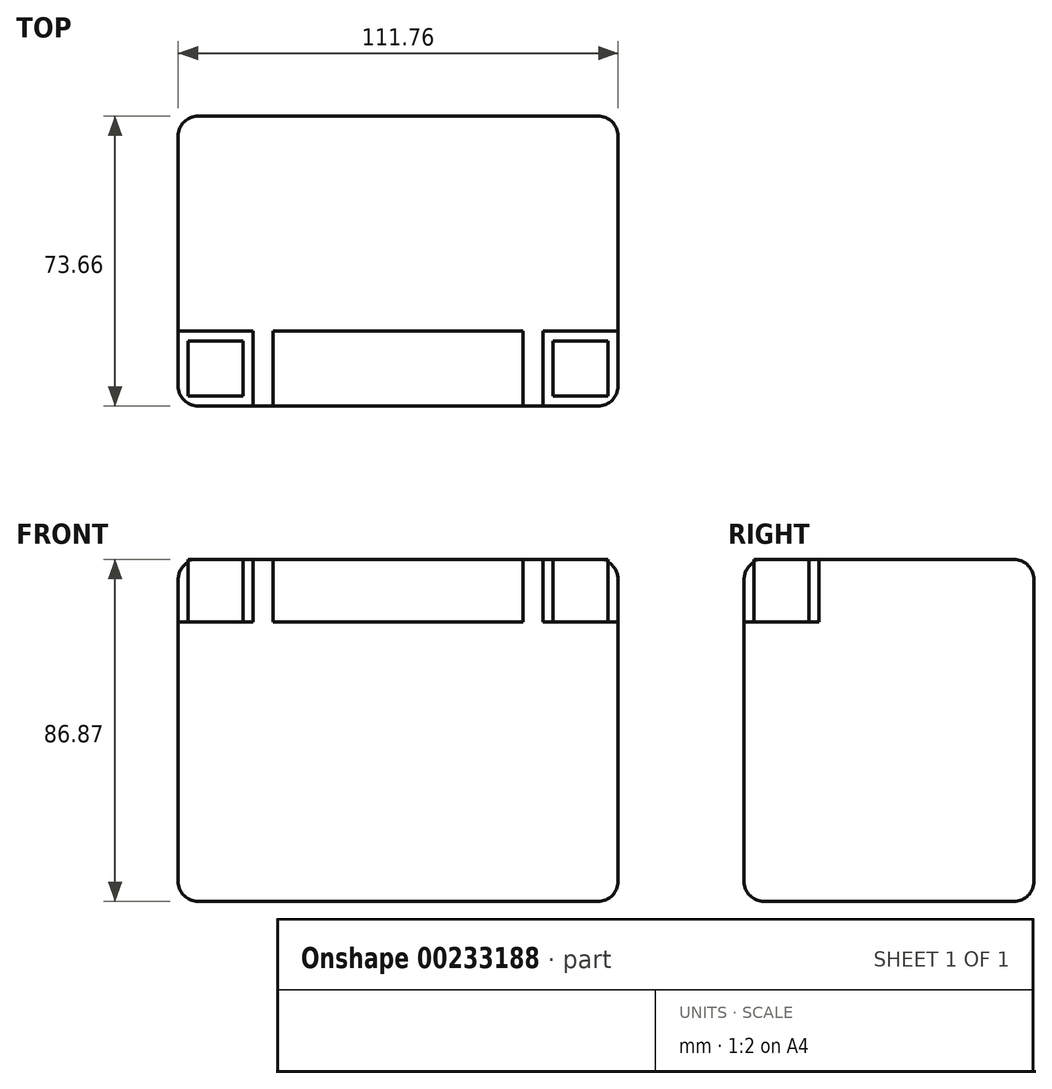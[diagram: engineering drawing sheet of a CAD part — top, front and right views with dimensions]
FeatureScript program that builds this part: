
annotation { "Feature Type Name" : "Feature", "Feature Type Description" : "" }
export const myFeature = defineFeature(function(context is Context, id is Id, definition is map)
    precondition{}
    {
        {
            var Q0;
            Q0=qCreatedBy(makeId("Top.planeOp"),FACE);
            var sketch = newSketch(context, id + "F0", { "sketchPlane" : qUnion([Q0])});
            skLineSegment(sketch, "E0.bottom", {"start": v(55.88, 36.83) * mm, "end": v(-55.88, 36.83) * mm});
            skLineSegment(sketch, "E0.top", {"start": v(55.88, -36.83) * mm, "end": v(-55.88, -36.83) * mm});
            skLineSegment(sketch, "E0.left", {"start": v(55.88, 36.83) * mm, "end": v(55.88, -36.83) * mm});
            skLineSegment(sketch, "E0.right", {"start": v(-55.88, 36.83) * mm, "end": v(-55.88, -36.83) * mm});
            skPoint(sketch, "E0.middle", {"position": v(0, 0) * mm});
            skSolve(sketch);
        }
        {
            var Q0;
            Q0 = qSketchRegion(id + "F0", true);
            extrude(context, id + "F1", {"entities" : qUnion([Q0]), "depth" : 86.87 * mm});
        }
        {
            var Q0;
            Q0=makeQuery(id+"F1.opExtrude","CAP_FACE",FACE,{"disambiguationData":[OSD([sQuery(id+"F0.wireOp",EDGE,"E0.bottom"),sQuery(id+"F0.wireOp",EDGE,"E0.top"),sQuery(id+"F0.wireOp",EDGE,"E0.left"),sQuery(id+"F0.wireOp",EDGE,"E0.right")])],"isStart":false});
            var sketch = newSketch(context, id + "F2", { "sketchPlane" : qUnion([Q0])});
            skLineSegment(sketch, "E1.bottom", {"start": v(-55.88, -36.83) * mm, "end": v(-36.83, -36.83) * mm});
            skLineSegment(sketch, "E1.top", {"start": v(-55.88, -17.78) * mm, "end": v(-36.83, -17.78) * mm});
            skLineSegment(sketch, "E1.left", {"start": v(-55.88, -36.83) * mm, "end": v(-55.88, -17.78) * mm});
            skLineSegment(sketch, "E1.right", {"start": v(-36.83, -36.83) * mm, "end": v(-36.83, -17.78) * mm});
            skLineSegment(sketch, "E2.bottom", {"start": v(-31.75, -36.83) * mm, "end": v(31.75, -36.83) * mm});
            skLineSegment(sketch, "E2.top", {"start": v(-31.75, -17.78) * mm, "end": v(31.75, -17.78) * mm});
            skLineSegment(sketch, "E2.left", {"start": v(-31.75, -36.83) * mm, "end": v(-31.75, -17.78) * mm});
            skLineSegment(sketch, "E2.right", {"start": v(31.75, -36.83) * mm, "end": v(31.75, -17.78) * mm});
            skLineSegment(sketch, "E3", {"start": v(0, 36.83) * mm, "end": v(0, -59.31) * mm, "construction": true});
            skPoint(sketch, "E3.endSnap0", {"position": v(0, -36.83) * mm});
            skLineSegment(sketch, "E4.bottom", {"start": v(-53.34, -34.3) * mm, "end": v(-39.37, -34.3) * mm});
            skLineSegment(sketch, "E4.top", {"start": v(-53.34, -20.32) * mm, "end": v(-39.37, -20.32) * mm});
            skLineSegment(sketch, "E4.left", {"start": v(-53.34, -34.3) * mm, "end": v(-53.34, -20.32) * mm});
            skLineSegment(sketch, "E4.right", {"start": v(-39.37, -34.3) * mm, "end": v(-39.37, -20.32) * mm});
            skLineSegment(sketch, "E5", {"start": v(-46.35, -17.78) * mm, "end": v(-46.35, -20.32) * mm, "construction": true});
            skLineSegment(sketch, "E6", {"start": v(-39.37, -27.3) * mm, "end": v(-36.83, -27.3) * mm, "construction": true});
            skLineSegment(sketch, "E7.MirrorCS", {"start": v(55.88, -17.78) * mm, "end": v(36.83, -17.78) * mm});
            skLineSegment(sketch, "E8.MirrorCS", {"start": v(36.83, -36.83) * mm, "end": v(36.83, -17.78) * mm});
            skLineSegment(sketch, "E9.MirrorCS", {"start": v(55.88, -36.83) * mm, "end": v(36.83, -36.83) * mm});
            skLineSegment(sketch, "E10.MirrorCS", {"start": v(55.88, -36.83) * mm, "end": v(55.88, -17.78) * mm});
            skLineSegment(sketch, "E11.MirrorCS", {"start": v(53.34, -34.29) * mm, "end": v(53.34, -20.32) * mm});
            skLineSegment(sketch, "E12.MirrorCS", {"start": v(53.34, -20.32) * mm, "end": v(39.37, -20.32) * mm});
            skLineSegment(sketch, "E13.MirrorCS", {"start": v(39.37, -34.29) * mm, "end": v(39.37, -20.32) * mm});
            skLineSegment(sketch, "E14.MirrorCS", {"start": v(53.34, -34.29) * mm, "end": v(39.37, -34.29) * mm});
            skSolve(sketch);
        }
        {
            var Q0;
            Q0 = qSketchRegion(id + "F2", true);
            extrude(context, id + "F3", {"entities" : qUnion([Q0]), "operationType" : NewBodyOperationType.REMOVE, "oppositeDirection" : true, "depth" : 15.88 * mm});
        }
        {
            var Q0;
            {var subQ0=sQuery(id+"F0.wireOp",EDGE,"E0.top");Q0=makeQuery(id+"F3.boolean.opBoolean","SPLIT",EDGE,{"disambiguationData":[TD([makeQuery(id+"F3.opExtrude","SWEPT_FACE",FACE,{"disambiguationData":[OSD([sQuery(id+"F2.wireOp",EDGE,"E1.right")])]})])],"derivedFrom":makeQuery(id+"F1.opExtrude","CAP_EDGE",EDGE,{"disambiguationData":[OSD([subQ0])],"isStart":false})});}
            var Q1;
            {var subQ0=sQuery(id+"F0.wireOp",EDGE,"E0.top");Q1=makeQuery(id+"F3.boolean.opBoolean","SPLIT",EDGE,{"disambiguationData":[TD([makeQuery(id+"F3.opExtrude","SWEPT_FACE",FACE,{"disambiguationData":[OSD([sQuery(id+"F2.wireOp",EDGE,"E2.right")])]})])],"derivedFrom":makeQuery(id+"F1.opExtrude","CAP_EDGE",EDGE,{"disambiguationData":[OSD([subQ0])],"isStart":false})});}
            var Q2;
            Q2=makeQuery(id+"F1.opExtrude","CAP_EDGE",EDGE,{"disambiguationData":[OSD([sQuery(id+"F0.wireOp",EDGE,"E0.left")])],"isStart":false});
            var Q3;
            Q3=makeQuery(id+"F1.opExtrude","CAP_EDGE",EDGE,{"disambiguationData":[OSD([sQuery(id+"F0.wireOp",EDGE,"E0.bottom")])],"isStart":false});
            var Q4;
            Q4=makeQuery(id+"F1.opExtrude","CAP_EDGE",EDGE,{"disambiguationData":[OSD([sQuery(id+"F0.wireOp",EDGE,"E0.right")])],"isStart":false});
            var Q5;
            Q5=makeQuery(id+"F1.opExtrude","SWEPT_EDGE",EDGE,{"disambiguationData":[OSD([sQuery(id+"F0.wireOp",EDGE,"E0.top"),sQuery(id+"F0.wireOp",EDGE,"E0.right")])]});
            var Q6;
            Q6=makeQuery(id+"F1.opExtrude","SWEPT_EDGE",EDGE,{"disambiguationData":[OSD([sQuery(id+"F0.wireOp",EDGE,"E0.top"),sQuery(id+"F0.wireOp",EDGE,"E0.left")])]});
            var Q7;
            Q7=makeQuery(id+"F1.opExtrude","SWEPT_EDGE",EDGE,{"disambiguationData":[OSD([sQuery(id+"F0.wireOp",EDGE,"E0.bottom"),sQuery(id+"F0.wireOp",EDGE,"E0.left")])]});
            var Q8;
            Q8=makeQuery(id+"F1.opExtrude","SWEPT_EDGE",EDGE,{"disambiguationData":[OSD([sQuery(id+"F0.wireOp",EDGE,"E0.bottom"),sQuery(id+"F0.wireOp",EDGE,"E0.right")])]});
            fillet(context, id + "F4", {"entities" : qUnion([Q0, Q1, Q2, Q3, Q4, Q5, Q6, Q7, Q8]), "radius" : 5.08 * mm, "tangentPropagation" : true, "allowEdgeOverflow" : false});
        }
        {
            var Q0;
            Q0=makeQuery(id+"F1.opExtrude","CAP_FACE",FACE,{"disambiguationData":[OSD([sQuery(id+"F0.wireOp",EDGE,"E0.bottom"),sQuery(id+"F0.wireOp",EDGE,"E0.top"),sQuery(id+"F0.wireOp",EDGE,"E0.left"),sQuery(id+"F0.wireOp",EDGE,"E0.right")])],"isStart":true});
            fillet(context, id + "F5", {"entities" : qUnion([Q0]), "radius" : 5.08 * mm, "tangentPropagation" : true, "allowEdgeOverflow" : false});
        }
    });
